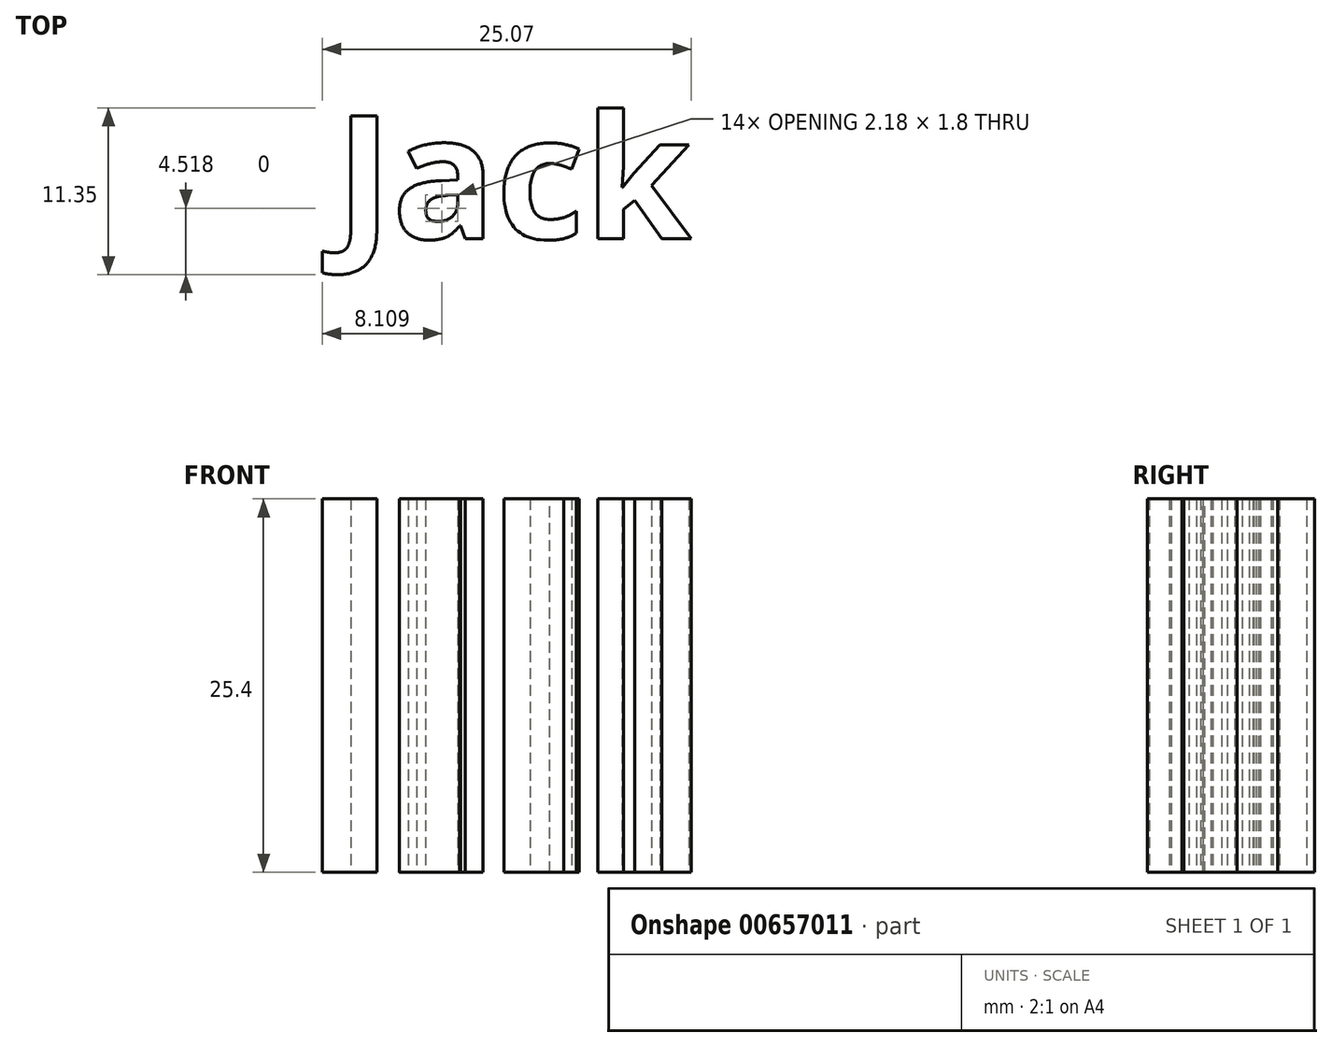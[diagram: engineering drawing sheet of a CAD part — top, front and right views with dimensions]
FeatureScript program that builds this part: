
annotation { "Feature Type Name" : "Feature", "Feature Type Description" : "" }
export const myFeature = defineFeature(function(context is Context, id is Id, definition is map)
    precondition{}
    {
        {
            var Q0;
            Q0=qCreatedBy(makeId("Top.planeOp"),FACE);
            var sketch = newSketch(context, id + "F0", { "sketchPlane" : qUnion([Q0])});
            skText(sketch, "E0", { "text": "Jack", "fontName": "OpenSans-Bold.ttf"});
            const initialGuessF0  = {"E0": [-0.02301, -0.00587, 1, 0, 0.00842]};
            skSetInitialGuess(sketch, initialGuessF0);
            skSolve(sketch);
        }
        {
            var Q0;
            Q0 = qSketchRegion(id + "F0", true);
            extrude(context, id + "F1", {"entities" : qUnion([Q0]), "depth" : 25.4 * mm, "offsetDistance" : 25.4 * mm});
        }
    });
